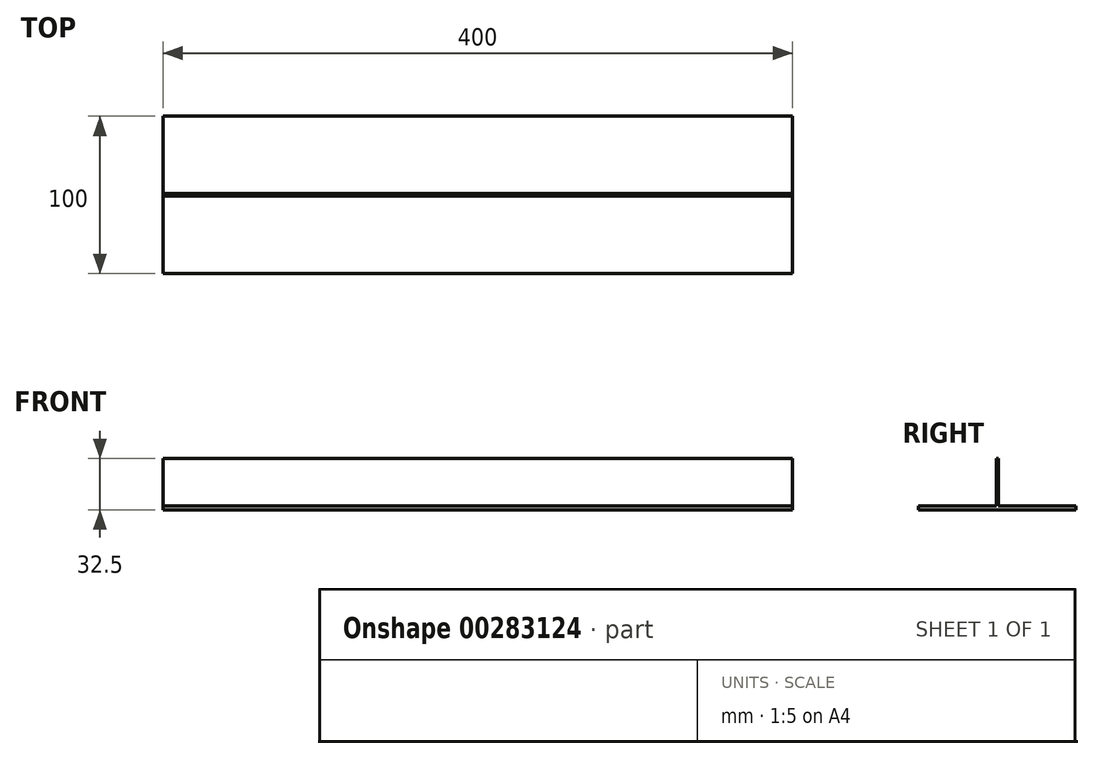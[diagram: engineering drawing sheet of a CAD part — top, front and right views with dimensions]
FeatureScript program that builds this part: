
annotation { "Feature Type Name" : "Feature", "Feature Type Description" : "" }
export const myFeature = defineFeature(function(context is Context, id is Id, definition is map)
    precondition{}
    {
        {
            assignVariable(context, id + "F0", {"name" : "t_plate", "anyValue" : 2.5});
        }
        {
            assignVariable(context, id + "F1", {"name" : "w_edge", "anyValue" : 30});
        }
        {
            var Q0;
            Q0=qCreatedBy(makeId("Top.planeOp"),FACE);
            var sketch = newSketch(context, id + "F2", { "sketchPlane" : qUnion([Q0])});
            skLineSegment(sketch, "E0.bottom", {"start": v(200, -50) * mm, "end": v(-200, -50) * mm});
            skLineSegment(sketch, "E0.top", {"start": v(200, 50) * mm, "end": v(-200, 50) * mm});
            skLineSegment(sketch, "E0.left", {"start": v(200, -50) * mm, "end": v(200, 50) * mm});
            skLineSegment(sketch, "E0.right", {"start": v(-200, -50) * mm, "end": v(-200, 50) * mm});
            skPoint(sketch, "E0.middle", {"position": v(0, 0) * mm});
            skSolve(sketch);
        }
        {
            var Q0;
            Q0 = qSketchRegion(id + "F2", true);
            extrude(context, id + "F3", {"entities" : qUnion([Q0]), "oppositeDirection" : true, "depth" : (getVariable(context, 't_plate')) * mm});
        }
        {
            var Q0;
            Q0=qCreatedBy(makeId("Top.planeOp"),FACE);
            var sketch = newSketch(context, id + "F4", { "sketchPlane" : qUnion([Q0])});
            skLineSegment(sketch, "E1.bottom", {"start": v(200, -0.75) * mm, "end": v(-200, -0.75) * mm});
            skLineSegment(sketch, "E1.top", {"start": v(200, 0.75) * mm, "end": v(-200, 0.75) * mm});
            skLineSegment(sketch, "E1.left", {"start": v(200, -0.75) * mm, "end": v(200, 0.75) * mm});
            skLineSegment(sketch, "E1.right", {"start": v(-200, -0.75) * mm, "end": v(-200, 0.75) * mm});
            skPoint(sketch, "E1.middle", {"position": v(0, 0) * mm});
            skSolve(sketch);
        }
        {
            var Q0;
            Q0 = qSketchRegion(id + "F4", true);
            extrude(context, id + "F5", {"entities" : qUnion([Q0]), "operationType" : NewBodyOperationType.ADD, "depth" : (getVariable(context, 'w_edge')) * mm});
        }
    });
